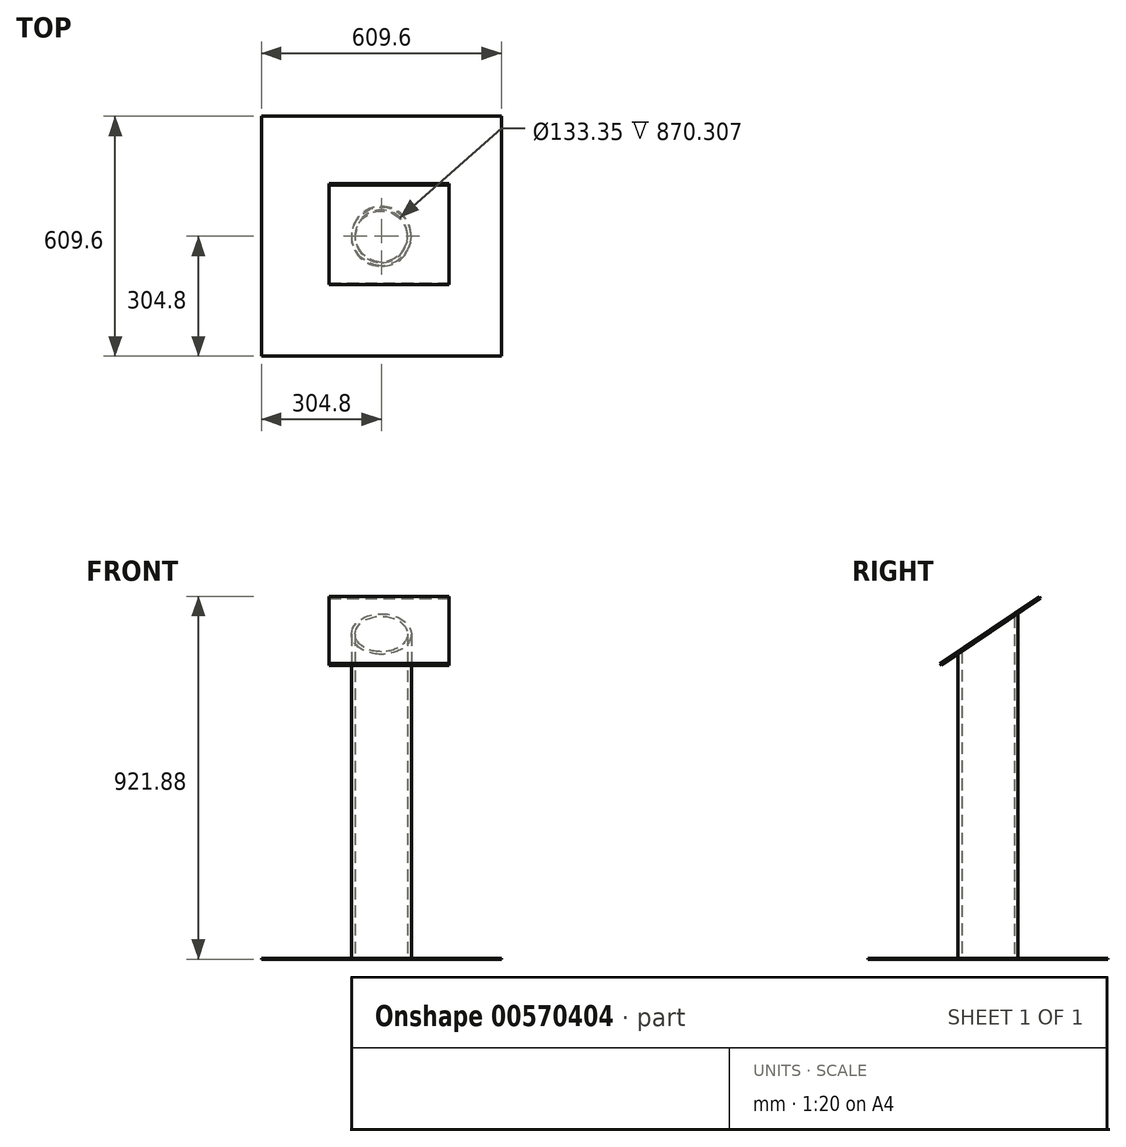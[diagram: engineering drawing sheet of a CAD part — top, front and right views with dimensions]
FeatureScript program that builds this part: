
annotation { "Feature Type Name" : "Feature", "Feature Type Description" : "" }
export const myFeature = defineFeature(function(context is Context, id is Id, definition is map)
    precondition{}
    {
        {
            var Q0;
            Q0=qCreatedBy(makeId("Top.planeOp"),FACE);
            var sketch = newSketch(context, id + "F0", { "sketchPlane" : qUnion([Q0])});
            skLineSegment(sketch, "E0.bottom", {"start": v(0, 0) * mm, "end": v(-609.6, 0) * mm});
            skLineSegment(sketch, "E0.top", {"start": v(0, 609.6) * mm, "end": v(-609.6, 609.6) * mm});
            skLineSegment(sketch, "E0.left", {"start": v(0, 0) * mm, "end": v(0, 609.6) * mm});
            skLineSegment(sketch, "E0.right", {"start": v(-609.6, 0) * mm, "end": v(-609.6, 609.6) * mm});
            skSolve(sketch);
        }
        {
            var Q0;
            Q0 = qSketchRegion(id + "F0", true);
            extrude(context, id + "F1", {"entities" : qUnion([Q0]), "depth" : 1.59 * mm, "offsetDistance" : 25.4 * mm});
        }
        {
            var Q0;
            Q0=makeQuery(id+"F1.opExtrude","CAP_FACE",FACE,{"disambiguationData":[OSD([sQuery(id+"F0.wireOp",EDGE,"E0.bottom"),sQuery(id+"F0.wireOp",EDGE,"E0.top"),sQuery(id+"F0.wireOp",EDGE,"E0.left"),sQuery(id+"F0.wireOp",EDGE,"E0.right")])],"isStart":false});
            var sketch = newSketch(context, id + "F2", { "sketchPlane" : qUnion([Q0])});
            skCircle(sketch, "E1", {"center": v(-304.8, 304.8) * mm, "radius": 76.2 * mm});
            skPoint(sketch, "E1.centerSnap0", {"position": v(-609.6, 304.8) * mm});
            skPoint(sketch, "E1.centerSnap1", {"position": v(-304.8, 609.6) * mm});
            skCircle(sketch, "E2", {"center": v(-304.8, 304.8) * mm, "radius": 66.68 * mm});
            skSolve(sketch);
        }
        {
            var Q0;
            Q0 = qSketchRegion(id + "F2", true);
            extrude(context, id + "F3", {"entities" : qUnion([Q0]), "operationType" : NewBodyOperationType.ADD, "depth" : 876.3 * mm, "offsetDistance" : 25.4 * mm, "hasSecondDirectionDraft" : true, "secondDirectionDraftAngle" : 45 * degree});
        }
        {
            var Q0;
            Q0=makeQuery(id+"F3.opExtrude","CAP_EDGE",EDGE,{"disambiguationData":[OSD([sQuery(id+"F2.wireOp",EDGE,"E2")])],"isStart":false});
            cPlane(context, id + "F4", {"entities" : qUnion([Q0]), "cplaneType" : CPlaneType.LINE_ANGLE, "offset" : 25.4 * mm, "angle" : 0 * degree, "width" : 152.4 * mm, "height" : 152.4 * mm});
        }
        {
            var Q0;
            Q0=qCreatedBy(id+"F4.planeOp",FACE);
            cPlane(context, id + "F5", {"entities" : qUnion([Q0]), "cplaneType" : CPlaneType.OFFSET, "offset" : 76.2 * mm, "width" : 152.4 * mm, "height" : 152.4 * mm});
        }
        {
            var Q0;
            Q0=qCreatedBy(id+"F5.planeOp",FACE);
            var sketch = newSketch(context, id + "F6", { "sketchPlane" : qUnion([Q0])});
            skLineSegment(sketch, "E3", {"start": v(228.57, 774.64) * mm, "end": v(389.24, 883.29) * mm});
            skLineSegment(sketch, "E4", {"start": v(389.24, 883.29) * mm, "end": v(228.57, 883.29) * mm});
            skLineSegment(sketch, "E5", {"start": v(228.57, 883.29) * mm, "end": v(228.57, 774.64) * mm});
            skSolve(sketch);
        }
        {
            var Q0;
            Q0 = qSketchRegion(id + "F6", true);
            extrude(context, id + "F7", {"entities" : qUnion([Q0]), "operationType" : NewBodyOperationType.REMOVE, "oppositeDirection" : true, "depth" : 152.4 * mm, "offsetDistance" : 25.4 * mm});
        }
        {
            var Q0;
            Q0=makeQuery(id+"F7.boolean.opBoolean","COPY",FACE,{"derivedFrom":makeQuery(id+"F7.opExtrude","SWEPT_FACE",FACE,{"disambiguationData":[OSD([sQuery(id+"F6.wireOp",EDGE,"E3")])]})});
            var sketch = newSketch(context, id + "F8", { "sketchPlane" : qUnion([Q0])});
            skLineSegment(sketch, "E6.bottom", {"start": v(-437.38, 571.92) * mm, "end": v(-132.58, 571.92) * mm});
            skLineSegment(sketch, "E6.top", {"start": v(-437.38, 876.72) * mm, "end": v(-132.58, 876.72) * mm});
            skLineSegment(sketch, "E6.left", {"start": v(-437.38, 571.92) * mm, "end": v(-437.38, 876.72) * mm});
            skLineSegment(sketch, "E6.right", {"start": v(-132.58, 571.92) * mm, "end": v(-132.58, 876.72) * mm});
            skSolve(sketch);
        }
        {
            var Q0;
            Q0 = qSketchRegion(id + "F8", true);
            extrude(context, id + "F9", {"entities" : qUnion([Q0]), "operationType" : NewBodyOperationType.ADD, "depth" : 6.35 * mm, "offsetDistance" : 25.4 * mm});
        }
    });
